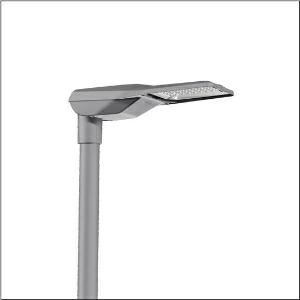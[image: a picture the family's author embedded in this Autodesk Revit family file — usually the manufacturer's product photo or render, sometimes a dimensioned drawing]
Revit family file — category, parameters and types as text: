
# Revit family: streetlight_sl_21_iq_mini___st1_0a_5xe2d31d08gb_54bd
name_source: partatom
category: Lighting Fixtures
units: mm (PartAtom-declared; Revit-internal decimal feet)

## family parameters
Cut with Voids When Loaded = No
Host = Face
Light Source = No
Part Type = Normal
Room Calculation Point = No
Round Connector Dimension = Use Diameter
Shared = No

## types (1)
- --- (1 x LED, 5680 lm, 37.1 W, 3000K)
    Apparent Load = 37 VA
    CIE Flux Codes = 37 72 97 100 100
    Color Rendering = 70
    Color Temperature = 3000K
    Default Elevation = 1800 mm
    Description = Streetlight SL 21 iQ mini, mast luminaire, primary light control with lens, of PMMA, primary optical cover: cover, of toughened safety glass, transparent, light distribution: ST1.0a, light emission: direct distribution, primary light characteristic: asymmetric, installation type: post-top, side-entry, LED, High Power LED, rated luminous flux: 5.680lm, luminous efficacy: 153lm/W, light colour: 730, colour temperature: 3000K, control: Auto-Match, Temp-Guard, Lumen-Switch, Night-Set, Smart-Wire, Light-Fading, Desk-Remote (wireless, voltage-free reading and setting of iQ features in the workshop via application-optimized NFC function/RFID function), optimised constant luminous flux control (CLO 2.0), presetting dimming linear, mains connection: 220..240V, AC, 50/60Hz, start of lifetime: 37W, end of service life: 39W, reduction: 18W, luminaire housing, of diecast aluminium, powder-coated, Siteco® metallic grey (DB 702S), corrosivity category C5 mid according to DIN EN ISO 12944, please order mast flange separately, inclination adjustable: 0°, 5°, 10°, 15°, sealing non-destructively replaceable, multi-level sealing system, length: 628mm, width: 235mm, height: 110mm, mast flange for spigot size: 42mm (side-entry): 5XC10008XM4, 60/48mm (side-entry/post-top): 5XC10108XM2, 76/60mm (side-entry/post-top): 5XC10108XM1, protection rating (complete): IP66, insulation class (complete): insulation class II (safety insulation), certification: CE, ENEC, ENEC+, VDE, impact resistance: IK09, permissible operating ambient temperature for outdoor applications: -40..+50°C, standard-compliant lighting for roads and squares, packaging unit: 1 piece

Light Distribution: ST1.0a
    Height = 110 mm
    Lamp = 1 x LED
    Lamp Light Flux = 5680 lm
    Lamp Power = 37.1 W
    Lamp count = 1
    Length = 625 mm
    Luminous efficacy = 153 lm/W
    Manufacturer = Siteco
    ModVariant = No
    Model = 5XE2D31D08GB
    Number of Poles = 1
    OnlyDefault = Yes
    Power Factor = 1
    Product Name = Streetlight SL 21 iQ mini | ST1.0a
    Product group = mast luminaire | pylon top
    ProductGroupID = 6100
    Protection Class = Protection class II
    Protection Degree = IP 66
    RLX_Detail_Level = 1
    RLX_Emergency_Light_Flux = 0 lm
    RLX_Emergency_Type = 0
    RLX_Emergency_Type_DB = No
    RlxData = <blob elided: 92229 chars, md5=ea2b8566>
    Socket = socket
    Standby Power = 0 W
    System Light Flux = 5680 lm
    System Power = 37 W
    Type Comments = factory setting: luminous flux: 100 % | dim-lin: 254 | 385 mA
    Type Image = l_1003519.jpg
    URL = http://relux.com
    VarID = @adj_122681
    Voltage = 0 V
    Weight = 0.00 kg
    Width = 234 mm

## geometry (parser evidence)
native form markers: Blend x4, Sweep x12
no freeform markers — native parametric forms only
